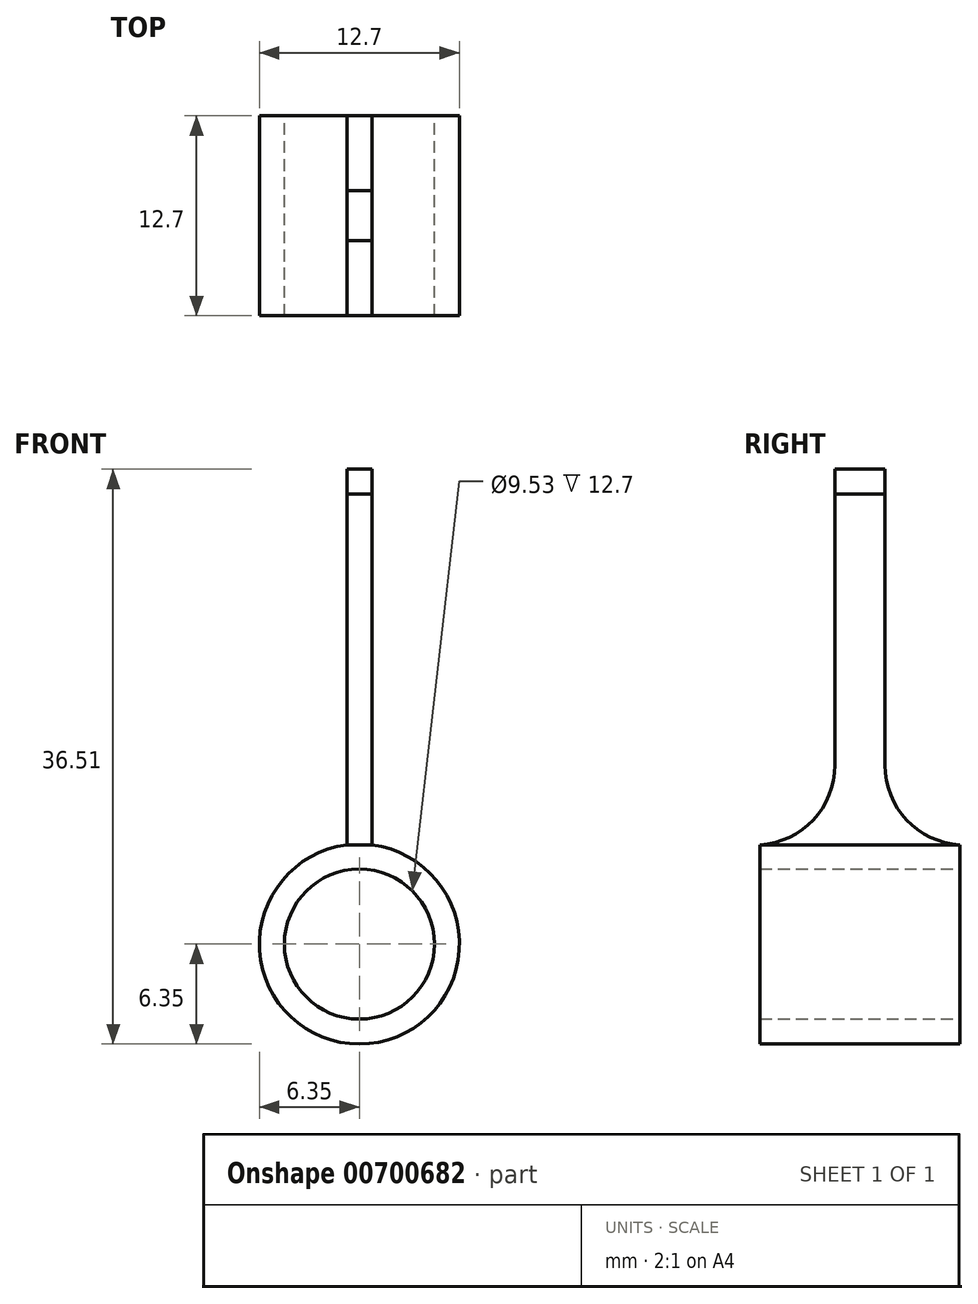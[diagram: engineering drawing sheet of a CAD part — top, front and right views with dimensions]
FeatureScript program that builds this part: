
annotation { "Feature Type Name" : "Feature", "Feature Type Description" : "" }
export const myFeature = defineFeature(function(context is Context, id is Id, definition is map)
    precondition{}
    {
        {
            var Q0;
            Q0=qCreatedBy(makeId("Front.planeOp"),FACE);
            var sketch = newSketch(context, id + "F0", { "sketchPlane" : qUnion([Q0])});
            skCircle(sketch, "E0", {"center": v(0, 0) * mm, "radius": 4.76 * mm});
            skCircle(sketch, "E1", {"center": v(0, 0) * mm, "radius": 6.35 * mm});
            skPoint(sketch, "E2", {"position": v(0, 6.35) * mm});
            skLineSegment(sketch, "E3.bottom", {"start": v(-0.8, 30.16) * mm, "end": v(0.8, 30.16) * mm});
            skLineSegment(sketch, "E3.top", {"start": v(-0.8, 4.76) * mm, "end": v(0.8, 4.76) * mm});
            skLineSegment(sketch, "E3.left", {"start": v(-0.8, 30.16) * mm, "end": v(-0.8, 4.76) * mm});
            skLineSegment(sketch, "E3.right", {"start": v(0.8, 30.16) * mm, "end": v(0.8, 4.76) * mm});
            skPoint(sketch, "E4", {"position": v(0, 4.76) * mm});
            skSolve(sketch);
        }
        {
            var Q0;
            Q0 = qSketchRegion(id + "F0", true);
            extrude(context, id + "F1", {"entities" : qUnion([Q0]), "depth" : 12.7 * mm, "offsetDistance" : 25.4 * mm});
        }
        {
            var Q0;
            Q0=makeQuery(id+"F1.opExtrude","SWEPT_FACE",FACE,{"disambiguationData":[OSD([sQuery(id+"F0.wireOp",EDGE,"E3.right")])]});
            var sketch = newSketch(context, id + "F2", { "sketchPlane" : qUnion([Q0])});
            skLineSegment(sketch, "E5", {"start": v(-7.94, 30.16) * mm, "end": v(-7.94, 6.3) * mm});
            skLineSegment(sketch, "E6", {"start": v(-4.76, 30.16) * mm, "end": v(-4.76, 6.3) * mm});
            skLineSegment(sketch, "E7", {"start": v(-4.76, 30.16) * mm, "end": v(-7.94, 30.16) * mm});
            skLineSegment(sketch, "E8", {"start": v(-7.94, 6.3) * mm, "end": v(-23.53, 6.3) * mm});
            skLineSegment(sketch, "E9", {"start": v(-23.53, 6.3) * mm, "end": v(-23.53, 42.43) * mm});
            skLineSegment(sketch, "E10", {"start": v(-23.53, 42.43) * mm, "end": v(8.45, 42.43) * mm});
            skLineSegment(sketch, "E11", {"start": v(8.45, 42.43) * mm, "end": v(8.45, 6.3) * mm});
            skLineSegment(sketch, "E12", {"start": v(8.45, 6.3) * mm, "end": v(-4.76, 6.3) * mm});
            skSolve(sketch);
        }
        {
            var Q0;
            Q0 = qSketchRegion(id + "F2", true);
            extrude(context, id + "F3", {"entities" : qUnion([Q0]), "operationType" : NewBodyOperationType.REMOVE, "oppositeDirection" : true, "depth" : 25.4 * mm, "offsetDistance" : 25.4 * mm});
        }
        {
            var Q0;
            Q0=makeQuery(id+"F3.boolean.opBoolean","COPY",EDGE,{"derivedFrom":makeQuery(id+"F3.opExtrude","SWEPT_EDGE",EDGE,{"disambiguationData":[OSD([sQuery(id+"F0.wireOp",EDGE,"E1"),sQuery(id+"F0.wireOp",EDGE,"E3.right"),sQuery(id+"F2.wireOp",EDGE,"E6"),sQuery(id+"F2.wireOp",EDGE,"E12")])]})});
            fillet(context, id + "F4", {"entities" : qUnion([Q0]), "radius" : 5.08 * mm, "tangentPropagation" : true, "allowEdgeOverflow" : false});
        }
        {
            var Q0;
            Q0=makeQuery(id+"F3.boolean.opBoolean","COPY",EDGE,{"derivedFrom":makeQuery(id+"F3.opExtrude","SWEPT_EDGE",EDGE,{"disambiguationData":[OSD([sQuery(id+"F0.wireOp",EDGE,"E1"),sQuery(id+"F0.wireOp",EDGE,"E3.right"),sQuery(id+"F2.wireOp",EDGE,"E5"),sQuery(id+"F2.wireOp",EDGE,"E8")])]})});
            fillet(context, id + "F5", {"entities" : qUnion([Q0]), "radius" : 5.08 * mm, "tangentPropagation" : true, "allowEdgeOverflow" : false});
        }
        {
            var Q0;
            Q0=makeQuery(id+"F3.boolean.opBoolean","COPY",FACE,{"derivedFrom":makeQuery(id+"F3.opExtrude","SWEPT_FACE",FACE,{"disambiguationData":[OSD([sQuery(id+"F2.wireOp",EDGE,"E6")])]})});
            var sketch = newSketch(context, id + "F6", { "sketchPlane" : qUnion([Q0])});
            skLineSegment(sketch, "E13.bottom", {"start": v(-0.8, 30.16) * mm, "end": v(0.8, 30.16) * mm});
            skLineSegment(sketch, "E13.top", {"start": v(-0.8, 28.58) * mm, "end": v(0.8, 28.58) * mm});
            skLineSegment(sketch, "E13.left", {"start": v(-0.8, 30.16) * mm, "end": v(-0.8, 28.58) * mm});
            skLineSegment(sketch, "E13.right", {"start": v(0.8, 30.16) * mm, "end": v(0.8, 28.58) * mm});
            skSolve(sketch);
        }
        {
            var Q0;
            Q0 = qSketchRegion(id + "F6", true);
            extrude(context, id + "F7", {"entities" : qUnion([Q0]), "operationType" : NewBodyOperationType.REMOVE, "oppositeDirection" : true, "depth" : 25.4 * mm, "offsetDistance" : 25.4 * mm});
        }
        {
            var Q0;
            Q0=makeQuery(id+"F7.boolean.opBoolean","COPY",FACE,{"derivedFrom":makeQuery(id+"F7.opExtrude","SWEPT_FACE",FACE,{"disambiguationData":[OSD([sQuery(id+"F6.wireOp",EDGE,"E13.top")])]})});
            var sketch = newSketch(context, id + "F8", { "sketchPlane" : qUnion([Q0])});
            skLineSegment(sketch, "E14.0", {"start": v(-0.8, -7.94) * mm, "end": v(-0.8, -4.76) * mm});
            skLineSegment(sketch, "E15.0", {"start": v(-0.8, -7.94) * mm, "end": v(0.8, -7.94) * mm});
            skLineSegment(sketch, "E16.0", {"start": v(0.8, -7.94) * mm, "end": v(0.8, -4.76) * mm});
            skLineSegment(sketch, "E17.0", {"start": v(0.8, -4.76) * mm, "end": v(-0.8, -4.76) * mm});
            skSolve(sketch);
        }
        {
            var Q0;
            Q0 = qSketchRegion(id + "F8", true);
            extrude(context, id + "F9", {"entities" : qUnion([Q0]), "depth" : 1.59 * mm, "offsetDistance" : 25.4 * mm});
        }
    });
